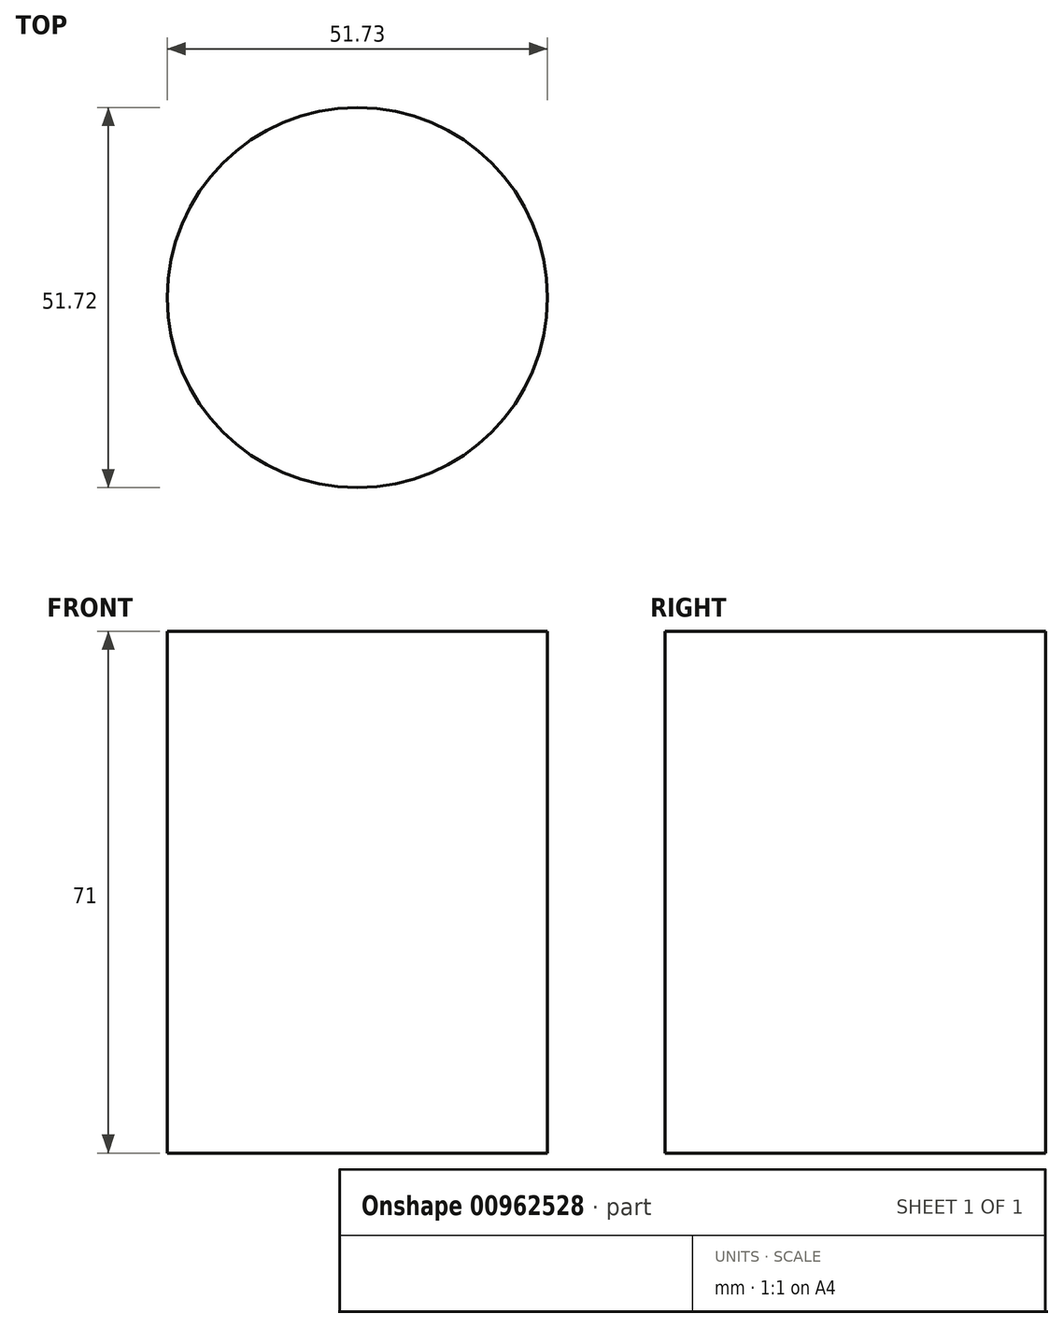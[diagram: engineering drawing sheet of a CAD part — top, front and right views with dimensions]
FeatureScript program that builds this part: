
annotation { "Feature Type Name" : "Feature", "Feature Type Description" : "" }
export const myFeature = defineFeature(function(context is Context, id is Id, definition is map)
    precondition{}
    {
        {
            var Q0;
            Q0=qCreatedBy(makeId("Top.planeOp"),FACE);
            var sketch = newSketch(context, id + "F0", { "sketchPlane" : qUnion([Q0])});
            skCircle(sketch, "E0", {"center": v(-38.13, 25.76) * mm, "radius": 25.86 * mm});
            skSolve(sketch);
        }
        {
            var Q0;
            Q0=makeQuery(id+"F0.imprint","IMPRINT",FACE,{"disambiguationData":[TD([[makeQuery(id+"F0.imprint","IMPRINT",EDGE,{"derivedFrom":sQuery(id+"F0.wireOp",EDGE,"E0")}),1.0]])]});
            extrude(context, id + "F1", {"entities" : qUnion([Q0]), "depth" : 71 * mm, "offsetDistance" : 25 * mm});
        }
    });
